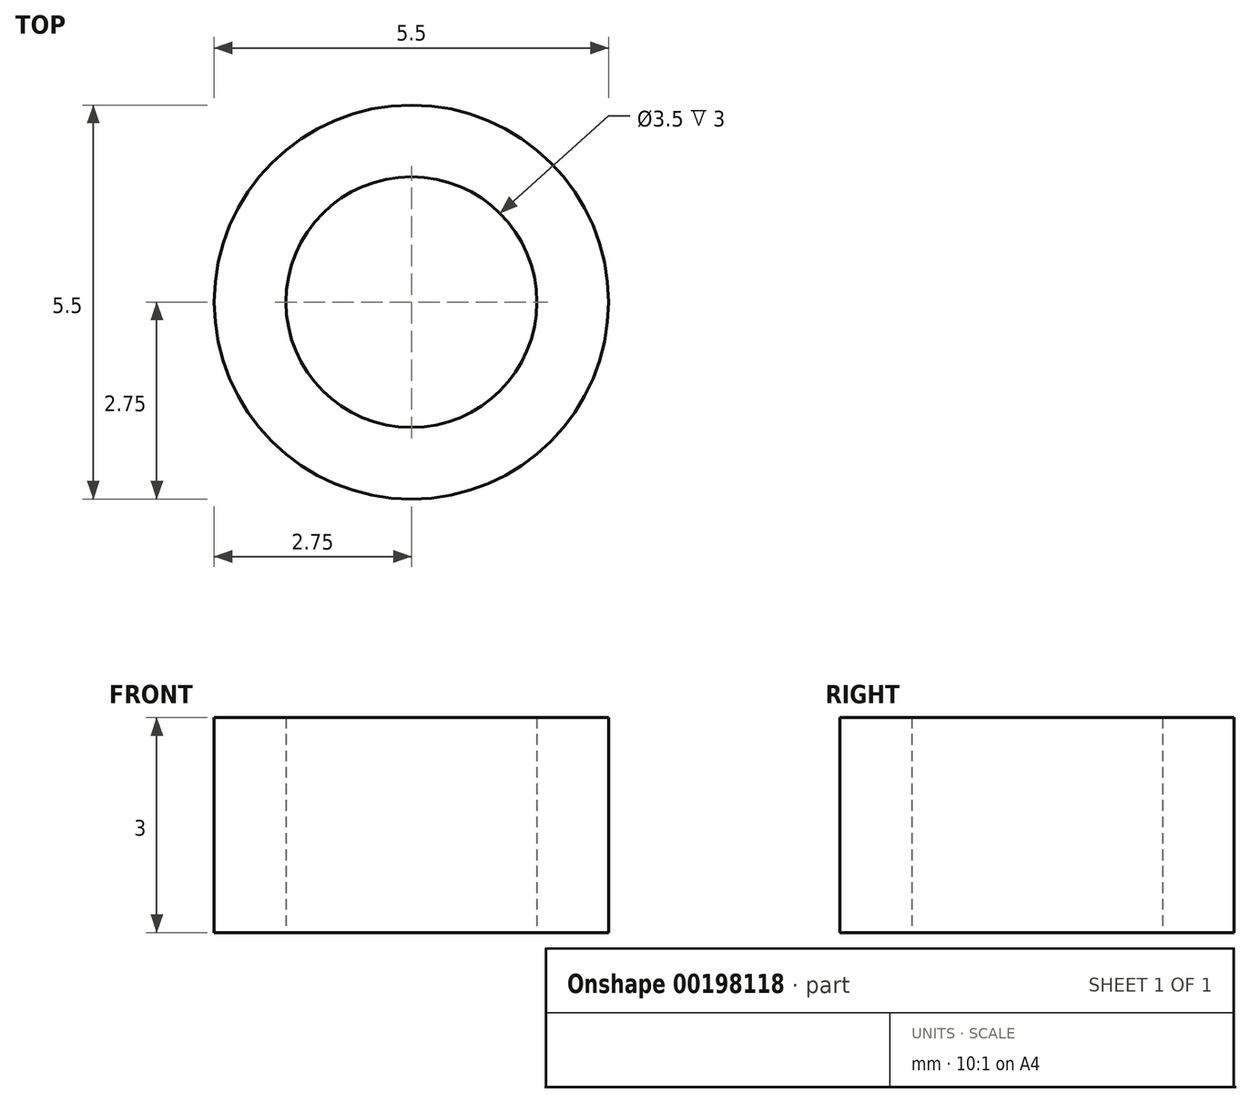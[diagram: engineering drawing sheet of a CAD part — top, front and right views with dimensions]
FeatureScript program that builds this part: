
annotation { "Feature Type Name" : "Feature", "Feature Type Description" : "" }
export const myFeature = defineFeature(function(context is Context, id is Id, definition is map)
    precondition{}
    {
        {
            var Q0;
            Q0=qCreatedBy(makeId("Top.planeOp"),FACE);
            var sketch = newSketch(context, id + "F0", { "sketchPlane" : qUnion([Q0])});
            skCircle(sketch, "E0", {"center": v(0, 0) * mm, "radius": 1.75 * mm});
            skCircle(sketch, "E1", {"center": v(0, 0) * mm, "radius": 2.75 * mm});
            skSolve(sketch);
        }
        {
            var Q0;
            Q0 = qSketchRegion(id + "F0", true);
            extrude(context, id + "F1", {"entities" : qUnion([Q0]), "depth" : 3 * mm});
        }
    });
